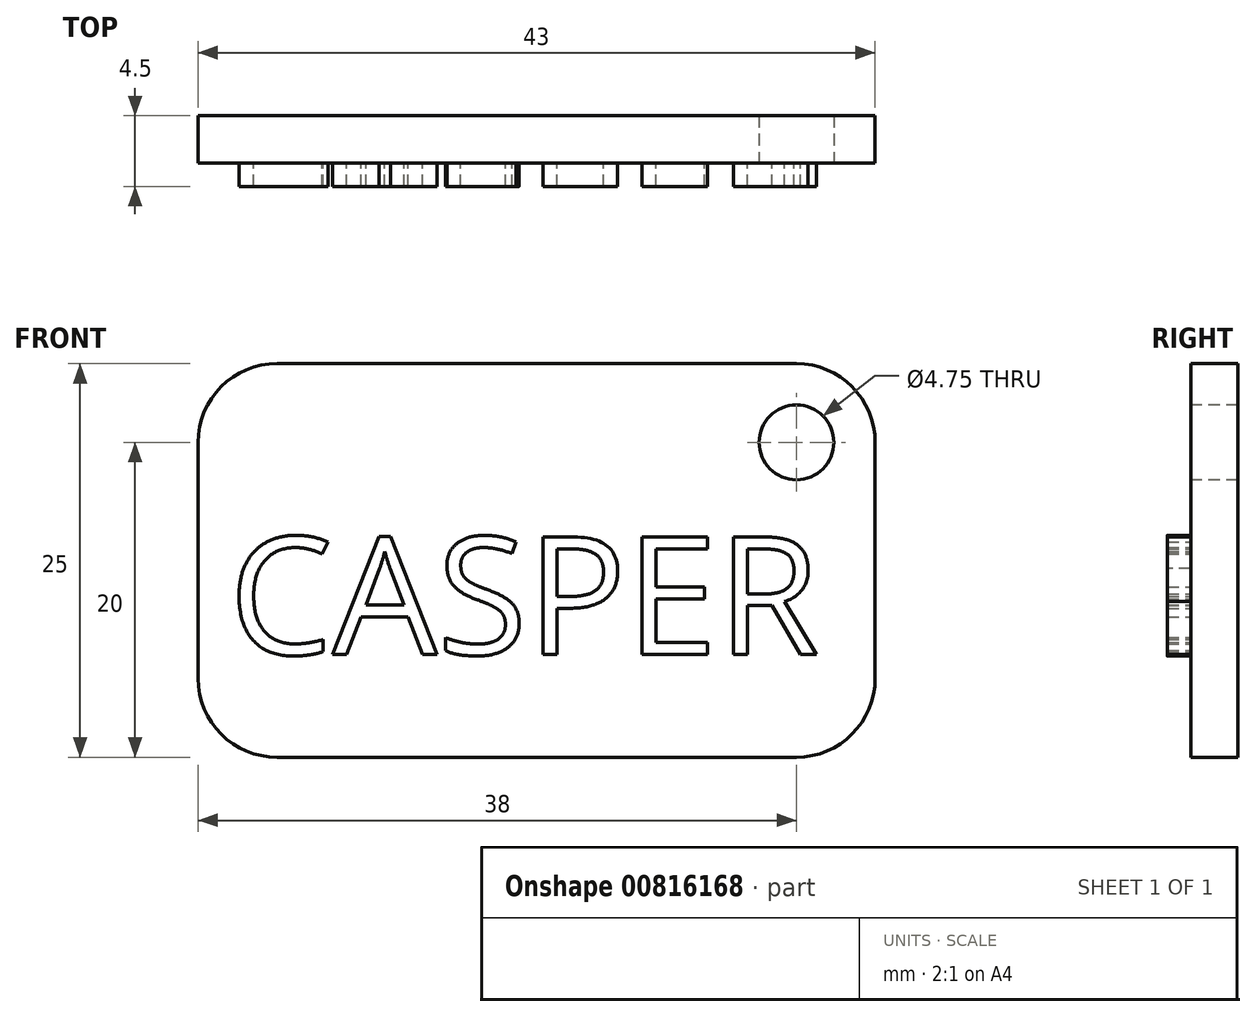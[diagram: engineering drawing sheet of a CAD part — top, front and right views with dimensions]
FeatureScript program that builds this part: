
annotation { "Feature Type Name" : "Feature", "Feature Type Description" : "" }
export const myFeature = defineFeature(function(context is Context, id is Id, definition is map)
    precondition{}
    {
        {
            var Q0;
            Q0=qCreatedBy(makeId("Front.planeOp"),FACE);
            var sketch = newSketch(context, id + "F0", { "sketchPlane" : qUnion([Q0])});
            skLineSegment(sketch, "E0.bottom", {"start": v(5, 0) * mm, "end": v(38, 0) * mm});
            skLineSegment(sketch, "E0.top", {"start": v(5, 25) * mm, "end": v(38, 25) * mm});
            skLineSegment(sketch, "E0.left", {"start": v(0, 5) * mm, "end": v(0, 20) * mm});
            skLineSegment(sketch, "E0.right", {"start": v(43, 5) * mm, "end": v(43, 20) * mm});
            skPoint(sketch, "E1.visualSharp", {"position": v(0, 25) * mm});
            skArc(sketch, "E1.filletArc", {"start": v(5, 25) * mm, "mid": v(1.46, 23.54) * mm, "end": v(0, 20) * mm});
            skPoint(sketch, "E2.visualSharp", {"position": v(0, 0) * mm});
            skArc(sketch, "E2.filletArc", {"start": v(0, 5) * mm, "mid": v(1.46, 1.46) * mm, "end": v(5, 0) * mm});
            skPoint(sketch, "E3.visualSharp", {"position": v(43, 0) * mm});
            skArc(sketch, "E3.filletArc", {"start": v(38, 0) * mm, "mid": v(41.54, 1.46) * mm, "end": v(43, 5) * mm});
            skPoint(sketch, "E4.visualSharp", {"position": v(43, 25) * mm});
            skArc(sketch, "E4.filletArc", {"start": v(43, 20) * mm, "mid": v(41.54, 23.54) * mm, "end": v(38, 25) * mm});
            skSolve(sketch);
        }
        {
            var Q0;
            Q0 = qSketchRegion(id + "F0", true);
            extrude(context, id + "F1", {"entities" : qUnion([Q0]), "depth" : 3 * mm, "offsetDistance" : 25 * mm});
        }
        {
            var Q0;
            Q0=makeQuery(id+"F1.opExtrude","CAP_FACE",FACE,{"disambiguationData":[OSD([sQuery(id+"F0.wireOp",EDGE,"E0.bottom"),sQuery(id+"F0.wireOp",EDGE,"E0.top"),sQuery(id+"F0.wireOp",EDGE,"E0.left"),sQuery(id+"F0.wireOp",EDGE,"E0.right"),sQuery(id+"F0.wireOp",EDGE,"E1.filletArc"),sQuery(id+"F0.wireOp",EDGE,"E2.filletArc"),sQuery(id+"F0.wireOp",EDGE,"E3.filletArc"),sQuery(id+"F0.wireOp",EDGE,"E4.filletArc")])],"isStart":false});
            var sketch = newSketch(context, id + "F2", { "sketchPlane" : qUnion([Q0])});
            skCircle(sketch, "E5", {"center": v(38, 20) * mm, "radius": 2.37 * mm});
            skSolve(sketch);
        }
        {
            var Q0;
            Q0 = qSketchRegion(id + "F2", true);
            extrude(context, id + "F3", {"entities" : qUnion([Q0]), "operationType" : NewBodyOperationType.REMOVE, "oppositeDirection" : true, "depth" : 3 * mm, "offsetDistance" : 25 * mm});
        }
        {
            var Q0;
            Q0=makeQuery(id+"F1.opExtrude","CAP_FACE",FACE,{"disambiguationData":[OSD([sQuery(id+"F0.wireOp",EDGE,"E0.bottom"),sQuery(id+"F0.wireOp",EDGE,"E0.top"),sQuery(id+"F0.wireOp",EDGE,"E0.left"),sQuery(id+"F0.wireOp",EDGE,"E0.right"),sQuery(id+"F0.wireOp",EDGE,"E1.filletArc"),sQuery(id+"F0.wireOp",EDGE,"E2.filletArc"),sQuery(id+"F0.wireOp",EDGE,"E3.filletArc"),sQuery(id+"F0.wireOp",EDGE,"E4.filletArc")])],"isStart":false});
            var sketch = newSketch(context, id + "F4", { "sketchPlane" : qUnion([Q0])});
            skText(sketch, "E6", { "text": "CASPER", "fontName": "OpenSans-Regular.ttf"});
            const initialGuessF4  = {"E6": [0.00196, 0.00653, 1, 0, 0.00752]};
            skSetInitialGuess(sketch, initialGuessF4);
            skSolve(sketch);
        }
        {
            var Q0;
            Q0 = qSketchRegion(id + "F4", true);
            extrude(context, id + "F5", {"entities" : qUnion([Q0]), "operationType" : NewBodyOperationType.ADD, "depth" : 1.5 * mm, "offsetDistance" : 25 * mm});
        }
    });
